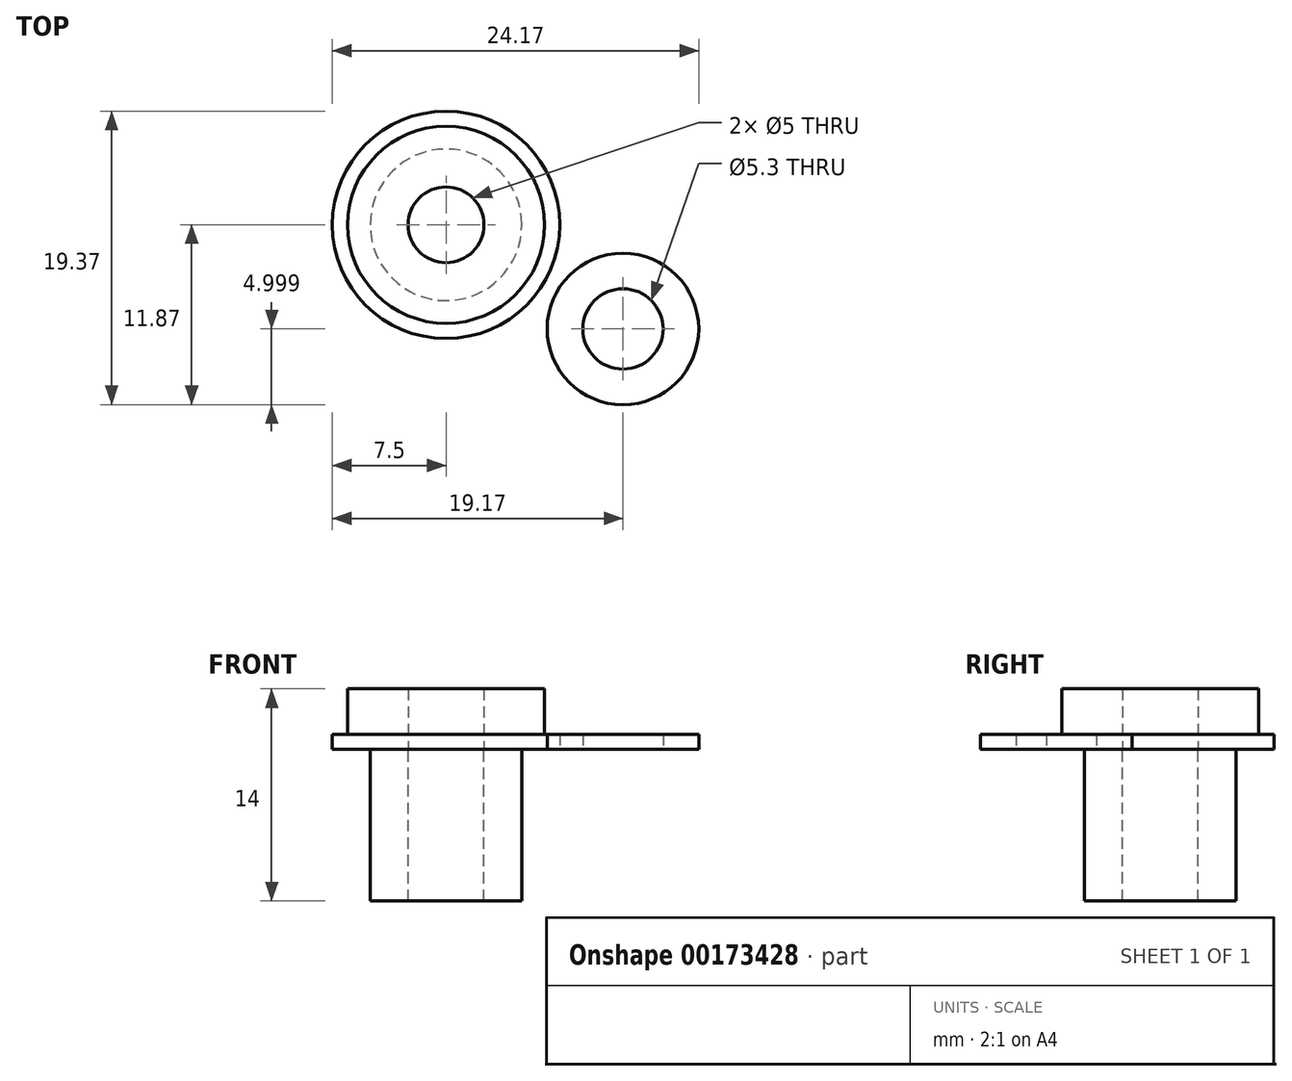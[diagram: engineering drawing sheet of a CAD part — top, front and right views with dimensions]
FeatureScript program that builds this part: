
annotation { "Feature Type Name" : "Feature", "Feature Type Description" : "" }
export const myFeature = defineFeature(function(context is Context, id is Id, definition is map)
    precondition{}
    {
        {
            var Q0;
            Q0=qCreatedBy(makeId("Top.planeOp"),FACE);
            var sketch = newSketch(context, id + "F0", { "sketchPlane" : qUnion([Q0])});
            skCircle(sketch, "E0", {"center": v(0, 0) * mm, "radius": 7.5 * mm});
            skCircle(sketch, "E1", {"center": v(0, 0) * mm, "radius": 6.5 * mm});
            skCircle(sketch, "E2", {"center": v(0, 0) * mm, "radius": 2.5 * mm});
            skSolve(sketch);
        }
        {
            var Q0;
            Q0=makeQuery(id+"F0.imprint","IMPRINT",FACE,{"disambiguationData":[TD([[makeQuery(id+"F0.imprint","IMPRINT",EDGE,{"derivedFrom":sQuery(id+"F0.wireOp",EDGE,"E0")}),1.0]])]});
            var Q1;
            Q1=makeQuery(id+"F0.imprint","IMPRINT",FACE,{"disambiguationData":[TD([[makeQuery(id+"F0.imprint","IMPRINT",EDGE,{"derivedFrom":sQuery(id+"F0.wireOp",EDGE,"E1")}),1.0]])]});
            extrude(context, id + "F1", {"entities" : qUnion([Q0, Q1]), "depth" : 1 * mm});
        }
        {
            var Q0;
            Q0=makeQuery(id+"F0.imprint","IMPRINT",FACE,{"disambiguationData":[TD([[makeQuery(id+"F0.imprint","IMPRINT",EDGE,{"derivedFrom":sQuery(id+"F0.wireOp",EDGE,"E1")}),1.0]])]});
            extrude(context, id + "F2", {"entities" : qUnion([Q0]), "operationType" : NewBodyOperationType.ADD, "depth" : 4 * mm});
        }
        {
            var Q0;
            Q0=makeQuery(id+"F1.opExtrude","CAP_FACE",FACE,{"disambiguationData":[OSD([sQuery(id+"F0.wireOp",EDGE,"E0")])],"isStart":true});
            var sketch = newSketch(context, id + "F3", { "sketchPlane" : qUnion([Q0])});
            skCircle(sketch, "E3.0", {"center": v(0, 0) * mm, "radius": 2.5 * mm});
            skCircle(sketch, "E4", {"center": v(0, 0) * mm, "radius": 5 * mm});
            skSolve(sketch);
        }
        {
            var Q0;
            Q0=qSketchRegion(id+"F3",true);
            extrude(context, id + "F4", {"entities" : qUnion([Q0]), "depth" : 10 * mm});
        }
        {
            var Q0;
            Q0=qCreatedBy(makeId("Top.planeOp"),FACE);
            var sketch = newSketch(context, id + "F5", { "sketchPlane" : qUnion([Q0])});
            skCircle(sketch, "E5", {"center": v(11.67, -6.87) * mm, "radius": 5 * mm});
            skCircle(sketch, "E6", {"center": v(11.67, -6.87) * mm, "radius": 2.65 * mm});
            skSolve(sketch);
        }
        {
            var Q0;
            Q0=qSketchRegion(id+"F5",true);
            extrude(context, id + "F6", {"entities" : qUnion([Q0]), "depth" : 1 * mm});
        }
    });
